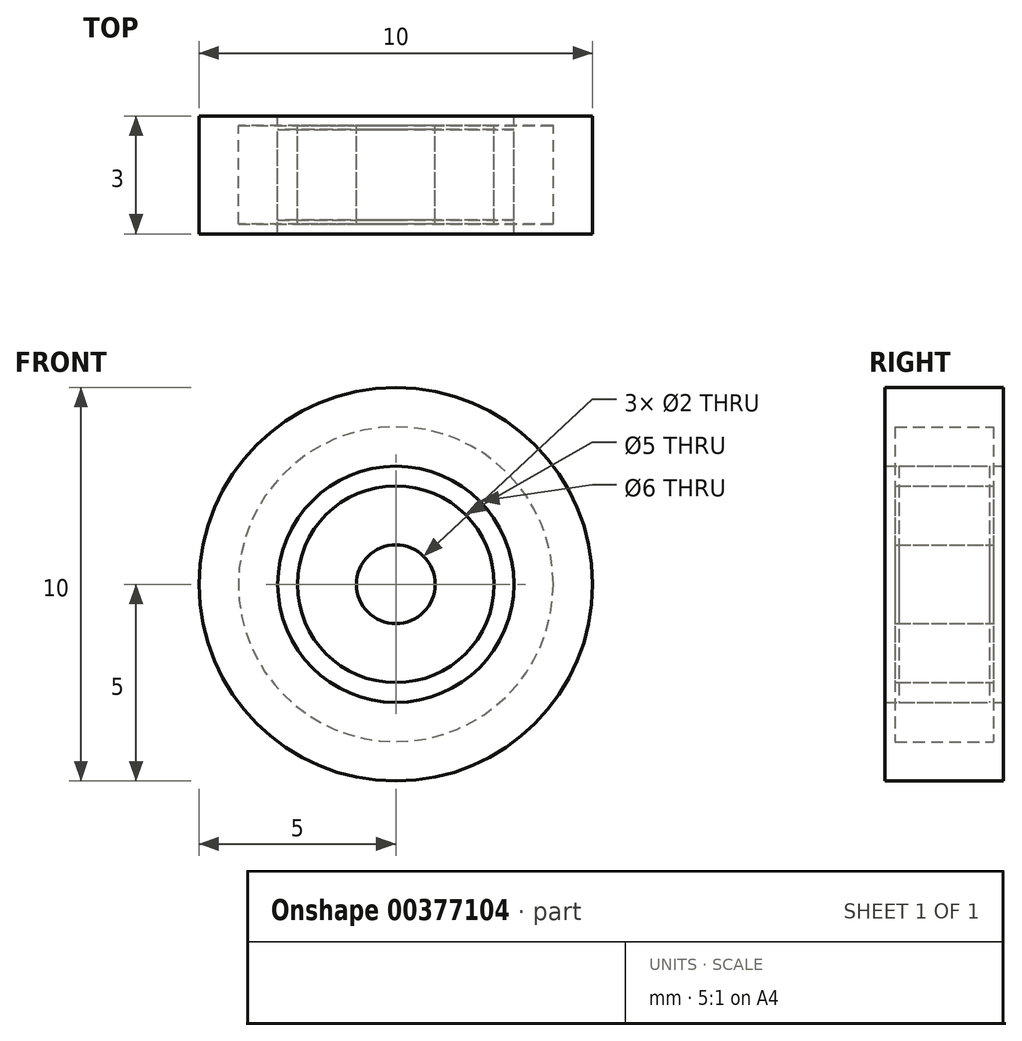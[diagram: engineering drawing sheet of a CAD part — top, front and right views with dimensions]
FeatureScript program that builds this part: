
annotation { "Feature Type Name" : "Feature", "Feature Type Description" : "" }
export const myFeature = defineFeature(function(context is Context, id is Id, definition is map)
    precondition{}
    {
        {
            var Q0;
            Q0=qCreatedBy(makeId("Top.planeOp"),FACE);
            var sketch = newSketch(context, id + "F0", { "sketchPlane" : qUnion([Q0])});
            skLineSegment(sketch, "E0.bottom", {"start": v(-3, 1.5) * mm, "end": v(-5, 1.5) * mm});
            skLineSegment(sketch, "E0.top", {"start": v(-3, -1.5) * mm, "end": v(-5, -1.5) * mm});
            skLineSegment(sketch, "E0.left", {"start": v(-3, 1.5) * mm, "end": v(-3, -1.5) * mm});
            skLineSegment(sketch, "E0.right", {"start": v(-5, 1.5) * mm, "end": v(-5, -1.5) * mm});
            skPoint(sketch, "E0.middle", {"position": v(-4, 0) * mm});
            skLineSegment(sketch, "E1", {"start": v(0, 1.5) * mm, "end": v(0, -1.5) * mm, "construction": true});
            skSolve(sketch);
        }
        {
            var Q0;
            Q0 = qSketchRegion(id + "F0", true);
            var Q1;
            Q1=sQuery(id+"F0.wireOp",EDGE,"E1");
            revolve(context, id + "F1", {"entities" : qUnion([Q0]), "axis" : qUnion([Q1]), "revolveType" : RevolveType.FULL});
        }
        {
            var Q0;
            Q0=qCreatedBy(makeId("Top.planeOp"),FACE);
            var sketch = newSketch(context, id + "F2", { "sketchPlane" : qUnion([Q0])});
            skLineSegment(sketch, "E2.bottom", {"start": v(-2.5, 1.25) * mm, "end": v(-4, 1.25) * mm});
            skLineSegment(sketch, "E2.top", {"start": v(-2.5, -1.25) * mm, "end": v(-4, -1.25) * mm});
            skLineSegment(sketch, "E2.left", {"start": v(-2.5, 1.25) * mm, "end": v(-2.5, -1.25) * mm});
            skLineSegment(sketch, "E2.right", {"start": v(-4, 1.25) * mm, "end": v(-4, -1.25) * mm});
            skPoint(sketch, "E2.middle", {"position": v(-3.25, 0) * mm});
            skLineSegment(sketch, "E3", {"start": v(0, 1.25) * mm, "end": v(0, -1.25) * mm, "construction": true});
            skSolve(sketch);
        }
        {
            var Q0;
            Q0 = qSketchRegion(id + "F2", true);
            var Q1;
            Q1=sQuery(id+"F2.wireOp",EDGE,"E3");
            revolve(context, id + "F3", {"entities" : qUnion([Q0]), "axis" : qUnion([Q1]), "revolveType" : RevolveType.FULL});
        }
        {
            var Q0;
            Q0=qCreatedBy(makeId("Top.planeOp"),FACE);
            var sketch = newSketch(context, id + "F4", { "sketchPlane" : qUnion([Q0])});
            skLineSegment(sketch, "E4.bottom", {"start": v(-1, 1.25) * mm, "end": v(-2.5, 1.25) * mm});
            skLineSegment(sketch, "E4.top", {"start": v(-1, -1.25) * mm, "end": v(-2.5, -1.25) * mm});
            skLineSegment(sketch, "E4.left", {"start": v(-1, 1.25) * mm, "end": v(-1, -1.25) * mm});
            skLineSegment(sketch, "E4.right", {"start": v(-2.5, 1.25) * mm, "end": v(-2.5, -1.25) * mm});
            skPoint(sketch, "E4.middle", {"position": v(-1.75, 0) * mm});
            skLineSegment(sketch, "E5", {"start": v(0, 1.25) * mm, "end": v(0, -1.25) * mm, "construction": true});
            skSolve(sketch);
        }
        {
            var Q0;
            Q0 = qSketchRegion(id + "F4", true);
            var Q1;
            Q1=sQuery(id+"F4.wireOp",EDGE,"E5");
            revolve(context, id + "F5", {"entities" : qUnion([Q0]), "axis" : qUnion([Q1]), "revolveType" : RevolveType.FULL});
        }
        {
            var Q0;
            Q0=qCreatedBy(makeId("Top.planeOp"),FACE);
            var sketch = newSketch(context, id + "F6", { "sketchPlane" : qUnion([Q0])});
            skLineSegment(sketch, "E6.bottom", {"start": v(-1, 1.15) * mm, "end": v(-2.5, 1.15) * mm});
            skLineSegment(sketch, "E6.top", {"start": v(-1, -1.15) * mm, "end": v(-2.5, -1.15) * mm});
            skLineSegment(sketch, "E6.left", {"start": v(-2.5, 1.15) * mm, "end": v(-2.5, -1.15) * mm});
            skLineSegment(sketch, "E6.right", {"start": v(-1, 1.15) * mm, "end": v(-1, -1.15) * mm});
            skPoint(sketch, "E6.middle", {"position": v(-1.75, 0) * mm});
            skLineSegment(sketch, "E7", {"start": v(0, 1.15) * mm, "end": v(0, -1.15) * mm, "construction": true});
            skSolve(sketch);
        }
        {
            var Q0;
            Q0 = qSketchRegion(id + "F6", true);
            var Q1;
            Q1=sQuery(id+"F6.wireOp",EDGE,"E7");
            revolve(context, id + "F7", {"entities" : qUnion([Q0]), "axis" : qUnion([Q1]), "revolveType" : RevolveType.FULL});
        }
        {
            var Q0;
            Q0=qCreatedBy(makeId("Top.planeOp"),FACE);
            var sketch = newSketch(context, id + "F8", { "sketchPlane" : qUnion([Q0])});
            skLineSegment(sketch, "E8.bottom", {"start": v(-1, 1.15) * mm, "end": v(-3, 1.15) * mm});
            skLineSegment(sketch, "E8.top", {"start": v(-1, -1.15) * mm, "end": v(-3, -1.15) * mm});
            skLineSegment(sketch, "E8.left", {"start": v(-1, 1.15) * mm, "end": v(-1, -1.15) * mm});
            skLineSegment(sketch, "E8.right", {"start": v(-3, 1.15) * mm, "end": v(-3, -1.15) * mm});
            skPoint(sketch, "E8.middle", {"position": v(-2, 0) * mm});
            skLineSegment(sketch, "E9", {"start": v(0, 1.15) * mm, "end": v(0, -1.15) * mm, "construction": true});
            skSolve(sketch);
        }
        {
            var Q0;
            Q0 = qSketchRegion(id + "F8", true);
            var Q1;
            Q1=sQuery(id+"F8.wireOp",EDGE,"E9");
            revolve(context, id + "F9", {"entities" : qUnion([Q0]), "axis" : qUnion([Q1]), "revolveType" : RevolveType.FULL});
        }
    });
